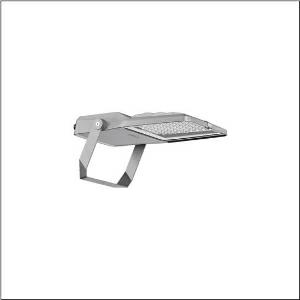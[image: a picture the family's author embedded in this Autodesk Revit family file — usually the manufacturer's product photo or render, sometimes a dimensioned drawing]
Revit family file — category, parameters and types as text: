
# Revit family: floodlight_fl_21_mini___pl33t_5xa7775b2f1a_fedb
name_source: partatom
category: Lighting Fixtures
units: mm (PartAtom-declared; Revit-internal decimal feet)

## family parameters
Cut with Voids When Loaded = No
Host = Face
Light Source = No
Part Type = Normal
Room Calculation Point = No
Round Connector Dimension = Use Diameter
Shared = No

## types (1)
- --- (1 x LED, 6150 lm, 45.7 W, 3000K)
    Apparent Load = 46 VA
    CIE Flux Codes = 26 75 99 100 100
    Color Rendering = 70
    Color Temperature = 3000K
    Default Elevation = 1800 mm
    Description = Floodlight FL 21 mini, floodlight, primary light control with lens, of PMMA, primary optical cover: protective disc, of toughened safety glass, transparent, light distribution: PL33T, light emission: direct distribution, installation type: surface-mounted, LED, High Power LED, rated luminous flux: 6.150lm, luminous efficacy: 135lm/W, light colour: 730, colour temperature: 3000K, control gear: ECG Smart Interface, control: flexible luminous flux parameterisation, time-dependent luminous flux control, constant luminous flux control, overheat protection, presetting dimming logarithmic, with terminal, 6-pole, mains connection: 220..240V, AC, 50/60Hz, start of lifetime: 46W, end of lifetime: 48W, reduction: 22W, luminaire housing, of diecast aluminium, powder-coated, Siteco® metallic grey (DB 702S), corrosivity category C5 according to DIN EN ISO 12944, mounting bracket, of steel, galvanised, powder-coated, Siteco® metallic grey (DB 702S), protection rating (complete): IP66, insulation class (complete): insulation class II (safety insulation), certification: CE, ENEC, VDE, protection symbol: D, impact resistance: IK08, permissible operating ambient temperature: -40..+40°C, permissible operating ambient temperature for outdoor applications: -40..+50°C, standard: DIN EN 12944, packaging unit: 1 piece

Light Distribution: PL33T
    Height = 70 mm
    Lamp = 1 x LED
    Lamp Light Flux = 6150 lm
    Lamp Power = 45.7 W
    Lamp count = 1
    Length = 485 mm
    Luminous efficacy = 135 lm/W
    Manufacturer = Siteco
    ModVariant = No
    Model = 5XA7775B2F1A
    Number of Poles = 1
    OnlyDefault = Yes
    Power Factor = 1
    Product Name = Floodlight FL 21 mini | PL33T
    Product group = floodlight | pylon top
    ProductGroupID = 6101
    Protection Class = Protection class II
    Protection Degree = IP 66
    RLX_Detail_Level = 1
    RlxData = <blob elided: 95761 chars, md5=390a7868>
    Socket = socket
    Standby Power = 0 W
    System Light Flux = 6150 lm
    System Power = 46 W
    Type Comments = factory setting: luminous flux: 100 % | dim-lin: 254 | 463 mA
    Type Image = l_1006845.jpg
    URL = http://relux.com
    VarID = @adj_058729
    Voltage = 0 V
    Weight = 0.00 kg
    Width = 337 mm

## geometry (parser evidence)
native form markers: Blend x4, Sweep x13
no freeform markers — native parametric forms only
